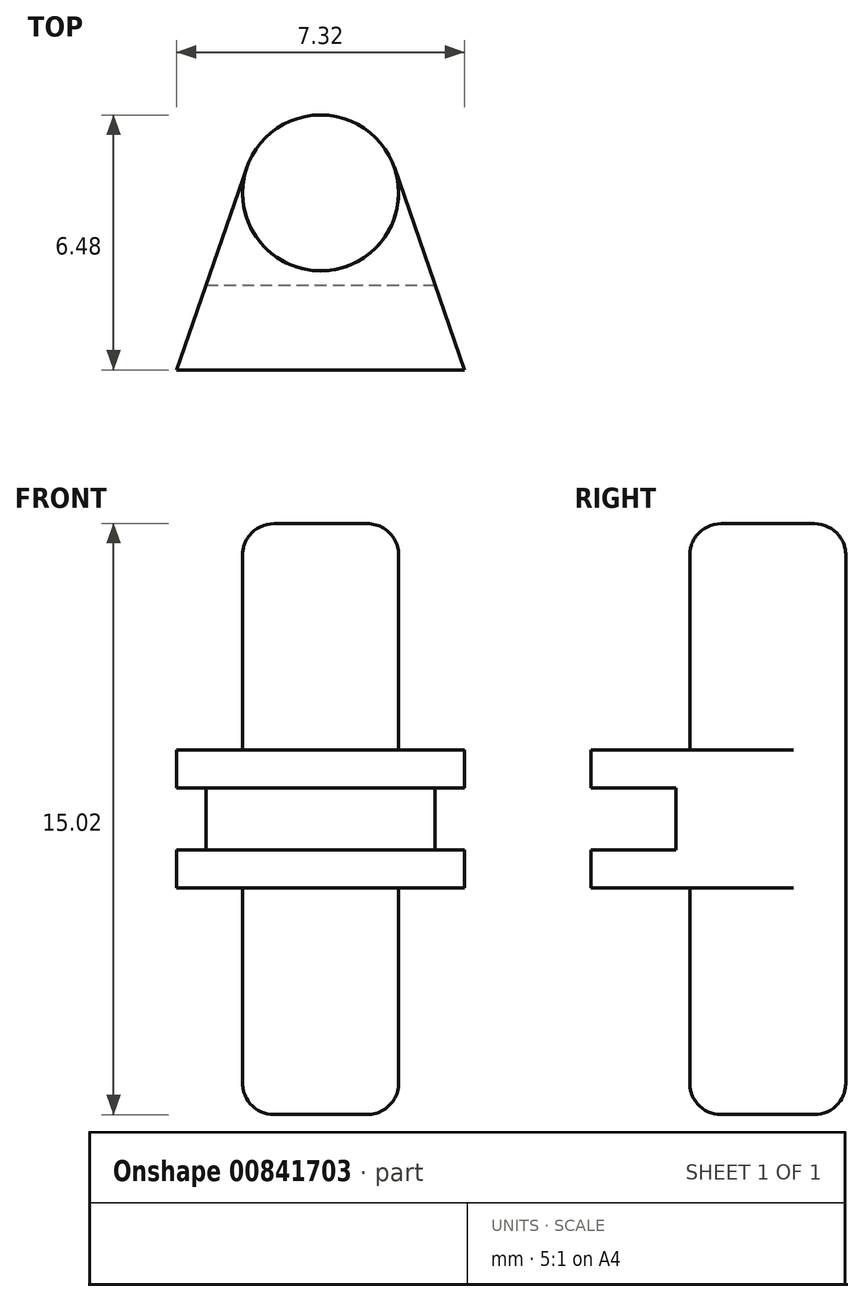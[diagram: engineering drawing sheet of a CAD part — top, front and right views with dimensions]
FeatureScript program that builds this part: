
annotation { "Feature Type Name" : "Feature", "Feature Type Description" : "" }
export const myFeature = defineFeature(function(context is Context, id is Id, definition is map)
    precondition{}
    {
        {
            var Q0;
            Q0=qCreatedBy(makeId("Top.planeOp"),FACE);
            var sketch = newSketch(context, id + "F0", { "sketchPlane" : qUnion([Q0])});
            skCircle(sketch, "E0", {"center": v(0, 0) * mm, "radius": 1.98 * mm});
            skSolve(sketch);
        }
        {
            var Q0;
            Q0 = qSketchRegion(id + "F0", true);
            extrude(context, id + "F1", {"entities" : qUnion([Q0]), "endBound" : BoundingType.SYMMETRIC, "depth" : 15 * mm, "offsetDistance" : 25.4 * mm});
        }
        {
            var Q0;
            Q0=qCreatedBy(makeId("Top.planeOp"),FACE);
            var sketch = newSketch(context, id + "F2", { "sketchPlane" : qUnion([Q0])});
            skLineSegment(sketch, "E1", {"start": v(-1.87, 0.65) * mm, "end": v(-3.66, -4.5) * mm});
            skLineSegment(sketch, "E2", {"start": v(-3.66, -4.5) * mm, "end": v(3.66, -4.5) * mm});
            skLineSegment(sketch, "E3", {"start": v(3.66, -4.5) * mm, "end": v(1.87, 0.65) * mm});
            skLineSegment(sketch, "E4", {"start": v(0, 0) * mm, "end": v(0, -4.5) * mm});
            skLineSegment(sketch, "E5", {"start": v(-1.87, 0.65) * mm, "end": v(1.87, 0.65) * mm});
            skSolve(sketch);
        }
        {
            var Q0;
            Q0 = qSketchRegion(id + "F2", true);
            extrude(context, id + "F3", {"entities" : qUnion([Q0]), "operationType" : NewBodyOperationType.ADD, "endBound" : BoundingType.SYMMETRIC, "depth" : 3.5 * mm, "offsetDistance" : 25.4 * mm});
        }
        {
            var Q0;
            Q0=makeQuery(id+"F3.opExtrude","SWEPT_FACE",FACE,{"disambiguationData":[OSD([sQuery(id+"F2.wireOp",EDGE,"E2")])]});
            var sketch = newSketch(context, id + "F4", { "sketchPlane" : qUnion([Q0])});
            skLineSegment(sketch, "E6.bottom", {"start": v(-3.66, 0.79) * mm, "end": v(3.66, 0.79) * mm});
            skLineSegment(sketch, "E6.top", {"start": v(-3.66, -0.79) * mm, "end": v(3.66, -0.79) * mm});
            skLineSegment(sketch, "E6.left", {"start": v(-3.66, 0.79) * mm, "end": v(-3.66, -0.79) * mm});
            skLineSegment(sketch, "E6.right", {"start": v(3.66, 0.79) * mm, "end": v(3.66, -0.79) * mm});
            skLineSegment(sketch, "E7", {"start": v(0, 1.75) * mm, "end": v(0, 0.79) * mm, "construction": true});
            skLineSegment(sketch, "E8", {"start": v(0, -1.75) * mm, "end": v(0, -0.79) * mm, "construction": true});
            skSolve(sketch);
        }
        {
            var Q0;
            Q0 = qSketchRegion(id + "F4", true);
            extrude(context, id + "F5", {"entities" : qUnion([Q0]), "operationType" : NewBodyOperationType.REMOVE, "oppositeDirection" : true, "depth" : 2.16 * mm, "offsetDistance" : 25.4 * mm});
        }
        {
            var Q0;
            Q0=makeQuery(id+"F1.opExtrude","CAP_EDGE",EDGE,{"disambiguationData":[OSD([sQuery(id+"F0.wireOp",EDGE,"E0")])],"isStart":false});
            var Q1;
            Q1=makeQuery(id+"F1.opExtrude","CAP_EDGE",EDGE,{"disambiguationData":[OSD([sQuery(id+"F0.wireOp",EDGE,"E0")])],"isStart":true});
            fillet(context, id + "F6", {"entities" : qUnion([Q0, Q1]), "radius" : 0.8 * mm, "tangentPropagation" : true, "allowEdgeOverflow" : false});
        }
    });
